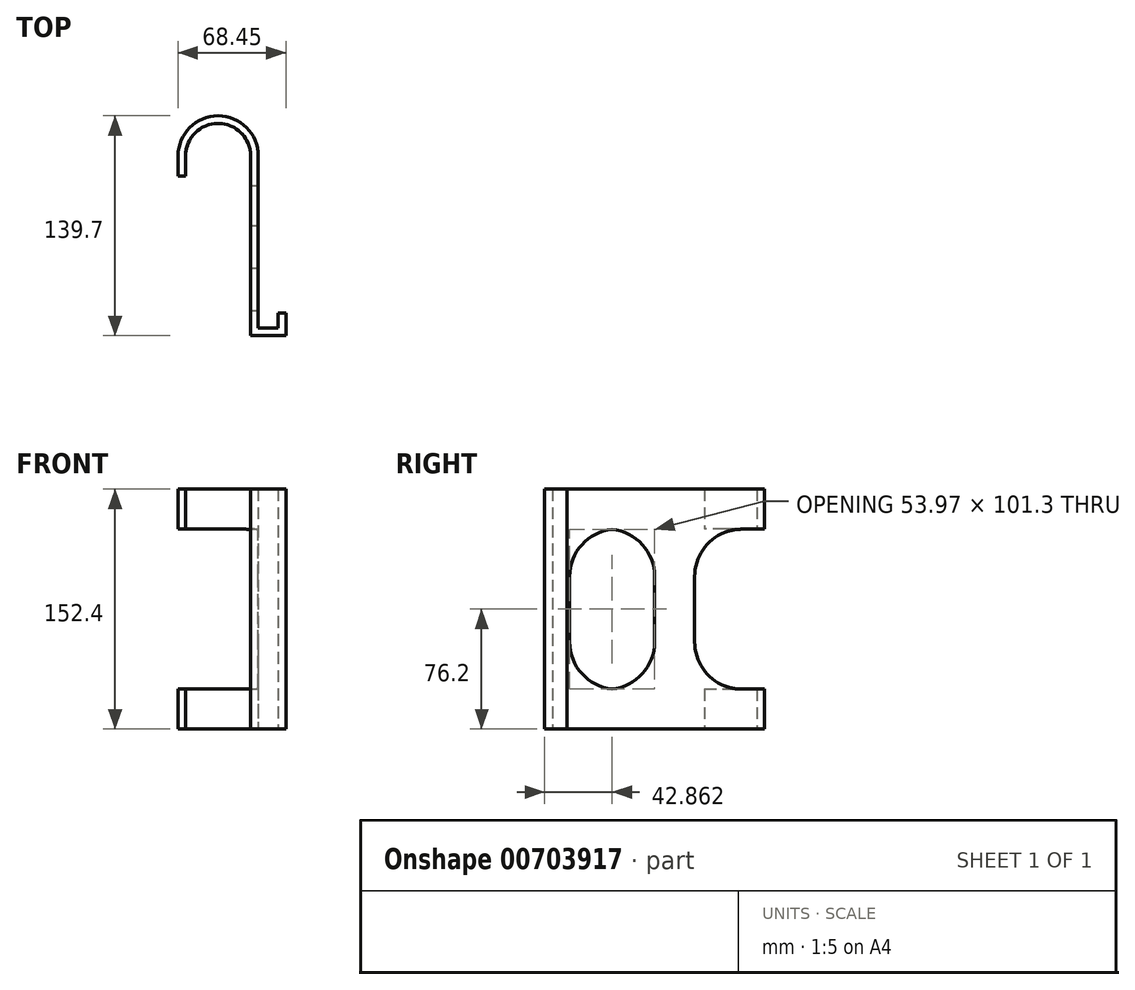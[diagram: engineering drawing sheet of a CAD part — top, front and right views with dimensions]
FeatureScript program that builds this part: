
annotation { "Feature Type Name" : "Feature", "Feature Type Description" : "" }
export const myFeature = defineFeature(function(context is Context, id is Id, definition is map)
    precondition{}
    {
        {
            var Q0;
            Q0=qCreatedBy(makeId("Top.planeOp"),FACE);
            var sketch = newSketch(context, id + "F0", { "sketchPlane" : qUnion([Q0])});
            skLineSegment(sketch, "E0", {"start": v(0, 0) * mm, "end": v(22.35, 0) * mm});
            skLineSegment(sketch, "E1", {"start": v(22.35, 0) * mm, "end": v(22.35, 14.35) * mm});
            skLineSegment(sketch, "E2", {"start": v(0, 0) * mm, "end": v(0, 114.24) * mm});
            skArc(sketch, "E3", {"start": v(0, 114.24) * mm, "mid": v(-20.64, 134.87) * mm, "end": v(-41.28, 114.24) * mm});
            skLineSegment(sketch, "E4", {"start": v(-41.28, 114.24) * mm, "end": v(-41.27, 101.54) * mm});
            skLineSegment(sketch, "E5.0", {"start": v(17.53, 4.83) * mm, "end": v(17.53, 14.35) * mm});
            skLineSegment(sketch, "E5.1", {"start": v(-46.1, 114.24) * mm, "end": v(-46.1, 101.54) * mm});
            skArc(sketch, "E5.2", {"start": v(4.83, 114.24) * mm, "mid": v(-20.64, 139.7) * mm, "end": v(-46.1, 114.24) * mm});
            skLineSegment(sketch, "E5.3", {"start": v(4.83, 4.83) * mm, "end": v(4.83, 114.24) * mm});
            skLineSegment(sketch, "E5.4", {"start": v(4.83, 4.83) * mm, "end": v(17.53, 4.83) * mm});
            skLineSegment(sketch, "E6", {"start": v(17.53, 14.35) * mm, "end": v(22.35, 14.35) * mm});
            skLineSegment(sketch, "E7", {"start": v(-46.1, 101.54) * mm, "end": v(-41.27, 101.54) * mm});
            skSolve(sketch);
        }
        {
            var Q0;
            Q0 = qSketchRegion(id + "F0", true);
            extrude(context, id + "F1", {"entities" : qUnion([Q0]), "endBound" : BoundingType.SYMMETRIC, "depth" : 152.4 * mm, "offsetDistance" : 25.4 * mm});
        }
        {
            var Q0;
            Q0=qCreatedBy(makeId("Right.planeOp"),FACE);
            var sketch = newSketch(context, id + "F2", { "sketchPlane" : qUnion([Q0])});
            skLineSegment(sketch, "E8", {"start": v(139.7, 50.8) * mm, "end": v(139.7, -50.8) * mm});
            skLineSegment(sketch, "E9", {"start": v(0, 0) * mm, "end": v(139.7, 0) * mm, "construction": true});
            skLineSegment(sketch, "E10", {"start": v(139.7, 50.8) * mm, "end": v(95.25, 50.8) * mm});
            skLineSegment(sketch, "E11", {"start": v(95.25, 50.8) * mm, "end": v(95.25, -50.8) * mm});
            skLineSegment(sketch, "E12", {"start": v(95.25, -50.8) * mm, "end": v(139.7, -50.8) * mm});
            skPoint(sketch, "E13.orphan", {"position": v(139.7, -76.2) * mm});
            skPoint(sketch, "E14.orphan", {"position": v(139.7, 76.2) * mm});
            skLineSegment(sketch, "E15.bottom", {"start": v(69.85, 50.8) * mm, "end": v(15.87, 50.8) * mm});
            skLineSegment(sketch, "E15.top", {"start": v(69.85, -50.8) * mm, "end": v(15.88, -50.8) * mm});
            skLineSegment(sketch, "E15.left", {"start": v(69.85, 50.8) * mm, "end": v(69.85, -50.8) * mm});
            skLineSegment(sketch, "E15.right", {"start": v(15.87, 50.8) * mm, "end": v(15.88, -50.8) * mm});
            skSolve(sketch);
        }
        {
            var Q0;
            Q0 = qSketchRegion(id + "F2", true);
            extrude(context, id + "F3", {"entities" : qUnion([Q0]), "operationType" : NewBodyOperationType.REMOVE, "endBound" : BoundingType.SYMMETRIC, "oppositeDirection" : true, "depth" : 254 * mm, "offsetDistance" : 25.4 * mm});
        }
        {
            var Q0;
            Q0=makeQuery(id+"F3.boolean.opBoolean","COPY",EDGE,{"derivedFrom":makeQuery(id+"F3.opExtrude","SWEPT_EDGE",EDGE,{"disambiguationData":[OSD([sQuery(id+"F2.wireOp",EDGE,"E15.bottom"),sQuery(id+"F2.wireOp",EDGE,"E15.right")])]})});
            var Q1;
            Q1=makeQuery(id+"F3.boolean.opBoolean","COPY",EDGE,{"derivedFrom":makeQuery(id+"F3.opExtrude","SWEPT_EDGE",EDGE,{"disambiguationData":[OSD([sQuery(id+"F2.wireOp",EDGE,"E15.bottom"),sQuery(id+"F2.wireOp",EDGE,"E15.left")])]})});
            var Q2;
            Q2=makeQuery(id+"F3.boolean.opBoolean","COPY",EDGE,{"derivedFrom":makeQuery(id+"F3.opExtrude","SWEPT_EDGE",EDGE,{"disambiguationData":[OSD([sQuery(id+"F2.wireOp",EDGE,"E15.top"),sQuery(id+"F2.wireOp",EDGE,"E15.right")])]})});
            var Q3;
            Q3=makeQuery(id+"F3.boolean.opBoolean","COPY",EDGE,{"derivedFrom":makeQuery(id+"F3.opExtrude","SWEPT_EDGE",EDGE,{"disambiguationData":[OSD([sQuery(id+"F2.wireOp",EDGE,"E15.top"),sQuery(id+"F2.wireOp",EDGE,"E15.left")])]})});
            var Q4;
            Q4=makeQuery(id+"F3.boolean.opBoolean","COPY",EDGE,{"derivedFrom":makeQuery(id+"F3.opExtrude","SWEPT_EDGE",EDGE,{"disambiguationData":[OSD([sQuery(id+"F2.wireOp",EDGE,"E10"),sQuery(id+"F2.wireOp",EDGE,"E11")])]})});
            var Q5;
            Q5=makeQuery(id+"F3.boolean.opBoolean","COPY",EDGE,{"derivedFrom":makeQuery(id+"F3.opExtrude","SWEPT_EDGE",EDGE,{"disambiguationData":[OSD([sQuery(id+"F2.wireOp",EDGE,"E11"),sQuery(id+"F2.wireOp",EDGE,"E12")])]})});
            fillet(context, id + "F4", {"entities" : qUnion([Q0, Q1, Q2, Q3, Q4, Q5]), "radius" : 30 * mm, "tangentPropagation" : true, "allowEdgeOverflow" : false});
        }
    });
